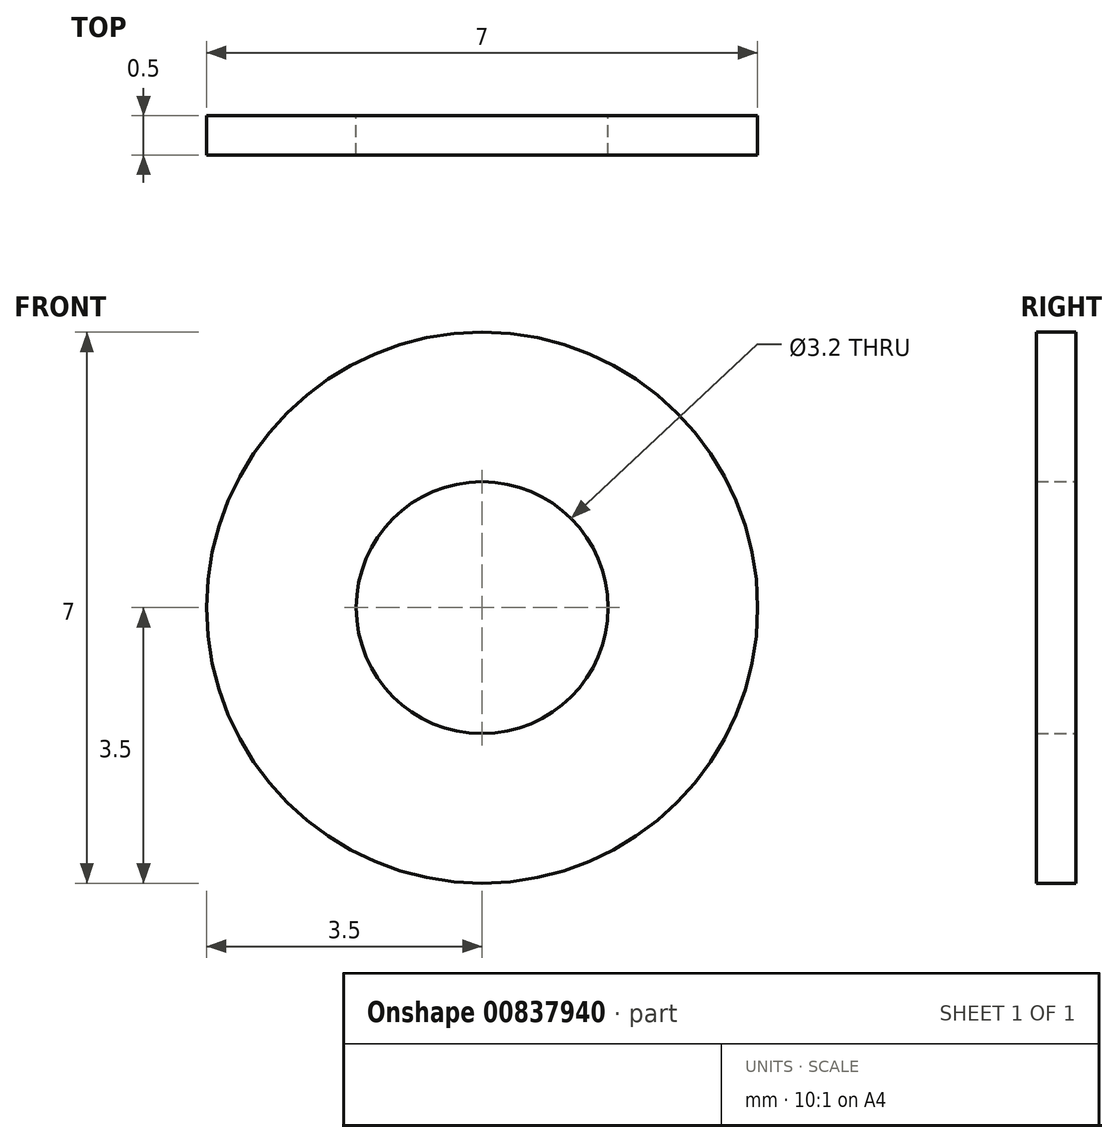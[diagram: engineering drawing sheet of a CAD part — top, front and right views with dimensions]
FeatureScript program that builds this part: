
annotation { "Feature Type Name" : "Feature", "Feature Type Description" : "" }
export const myFeature = defineFeature(function(context is Context, id is Id, definition is map)
    precondition{}
    {
        {
            var Q0;
            Q0=qCreatedBy(makeId("Front.planeOp"),FACE);
            var sketch = newSketch(context, id + "F0", { "sketchPlane" : qUnion([Q0])});
            skCircle(sketch, "E0", {"center": v(0, 0) * mm, "radius": 1.6 * mm});
            skCircle(sketch, "E1", {"center": v(0, 0) * mm, "radius": 3.5 * mm});
            skSolve(sketch);
        }
        {
            var Q0;
            Q0=makeQuery(id+"F0.imprint","IMPRINT",FACE,{"disambiguationData":[TD([[makeQuery(id+"F0.imprint","IMPRINT",EDGE,{"derivedFrom":sQuery(id+"F0.wireOp",EDGE,"E0")}),-1.0]])]});
            extrude(context, id + "F1", {"entities" : qUnion([Q0]), "depth" : 0.5 * mm, "offsetDistance" : 25 * mm});
        }
    });
